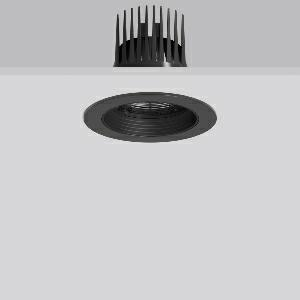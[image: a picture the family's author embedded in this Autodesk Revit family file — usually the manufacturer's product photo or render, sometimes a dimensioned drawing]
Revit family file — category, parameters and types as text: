
# Revit family: heledon_maxi_e_901776_003_76_0d9c
name_source: partatom
category: Lighting Fixtures
units: mm (PartAtom-declared; Revit-internal decimal feet)

## family parameters
Cut with Voids When Loaded = No
Host = Face
Light Source = No
Part Type = Normal
Room Calculation Point = No
Round Connector Dimension = Use Diameter
Shared = No

## types (1)
- HELEDON maxi E (1 x LED Modul 932 fresh meat, 1800 lm, 3200)
    Apparent Load = 33 VA
    Approval mark = CE
    CIE Flux Codes = 96 99 100 100 100
    Color Rendering = 90
    Color Temperature = 3200
    Default Elevation = 1800 mm  [stored 5.90551 ft]
    Description = Series: HELEDON maxi
Round recessed downlight. Housing: die-cast aluminium, powder-coated. Black plastic ring and recessed LED to prevent glare from the side. Optical assembly with lens made of plastic (polycarbonate) for the best homogeneous light distribution - can be changed without tools. Special LED for illumination of meat included. Suitable for Recessed ceiling mounting. Installation without tools thanks to spring fastening system. Including separate LED converter with connecting cable 600 mm.High quality converter without flickering and stroboscopic effect. Through-wiring box (5 pole) available as accessory. The following accessories can be mounted without use of tools: interchangeable lenses, decorative glasses, honeycomb louvre, clear and frosted diffusers, white interchangeable plastic ring. 
Colour: deep black, matt (RAL 9005)
Diameter: 162 mm
Height: 3 mm
Cut-out diameter: 152 mm
Recess height: 200 mm
Luminaire: recess height: 135 mm
Lamp: LED
Socket: without socket
Colour temperature: fresh meat
System power: 33 W
Rated luminous flux: 1800 lm
Luminous efficiency: 55 lm/W
Control gear: Converter, dimmable, DALI
Protection class: II
Type of protection: IP 20
    Height = 0 mm  [stored 0 ft]
    Lamp = 1 x LED Modul 932 fresh meat
    Lamp Light Flux = 1800 lm
    Lamp count = 1
    Length = 162 mm
    Lifetime = 50000 h
    Luminous efficacy = 55 lm/W
    Manufacturer = RZB
    ModVariant = No
    Model = 901776.003.76
    Mounting Place = Ceiling
    Mounting Type = Recessed
    Number of Poles = 1
    OnlyDefault = Yes
    Power Factor = 1
    Product Name = HELEDON maxi E
    Product group = Recessed downlights
    ProductGroupID = 402
    Protection Class = Protection class II
    Protection Degree = IP 20
    RLX_Detail_Level = 1
    RLX_Emergency_Light_Flux = 0 lm
    RLX_Emergency_Type = 0
    RLX_Emergency_Type_DB = No
    RlxData = <blob elided: 122189 chars, md5=57206b06>
    Socket = socket
    Standby Power = 0 W
    System Light Flux = 1800 lm
    System Power = 33 W
    Type Comments = Product without accessories
    Type Image = 901663.003.jpg
    URL = http://relux.com
    VarID = ---
    Voltage = 230 V
    Voltage Range = 220-240 V
    Weight = 0.00 kg
    Width = 0 mm  [stored 0 ft]

note: [stored X ft] marks values corroborated as IEEE doubles in the binary element streams (Revit-internal decimal feet)

## geometry (parser evidence)
native form markers: Blend x4, Sweep x13
no freeform markers — native parametric forms only
